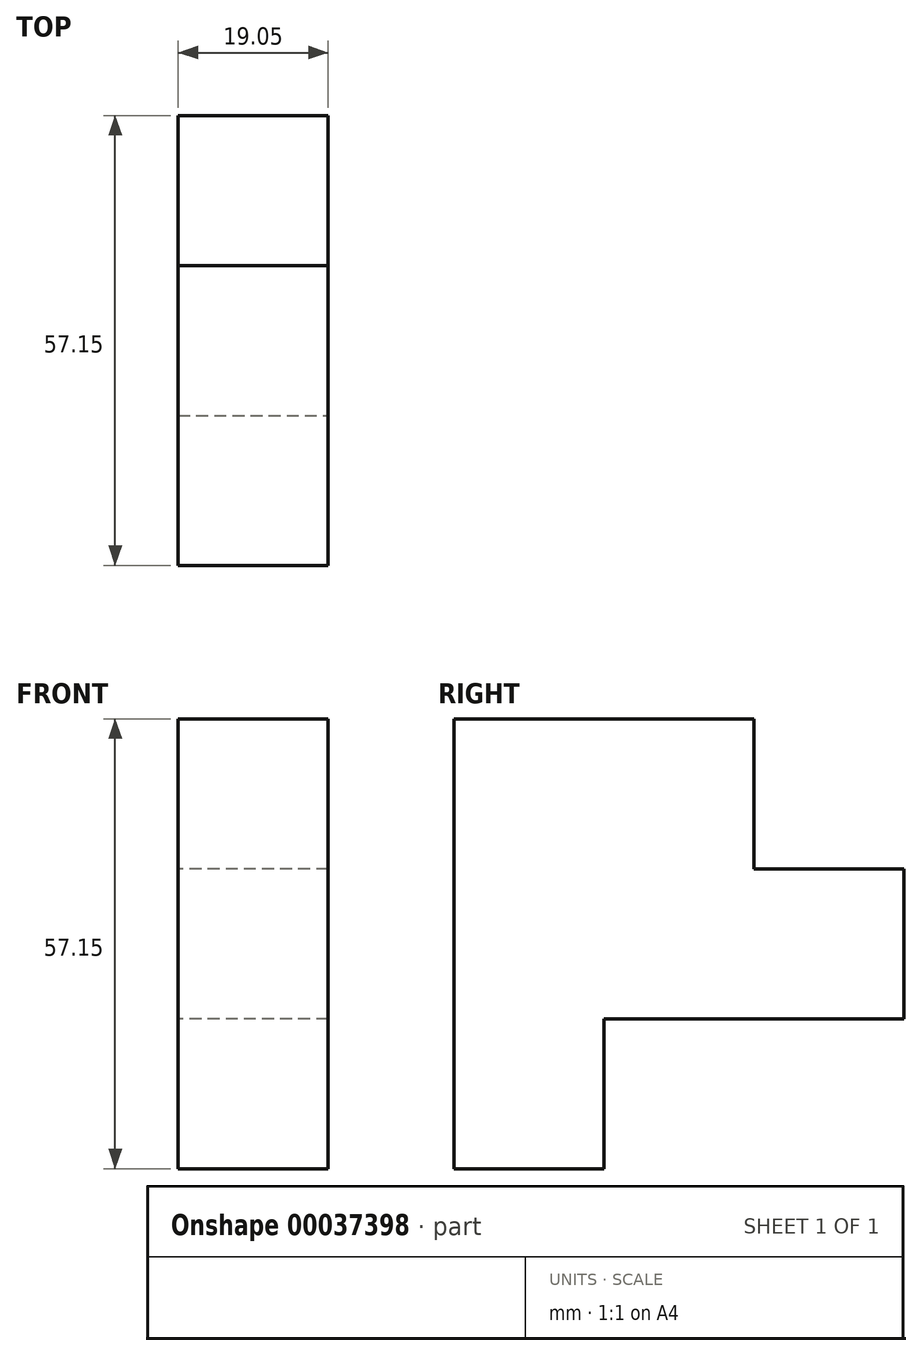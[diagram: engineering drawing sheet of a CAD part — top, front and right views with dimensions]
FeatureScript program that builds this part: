
annotation { "Feature Type Name" : "Feature", "Feature Type Description" : "" }
export const myFeature = defineFeature(function(context is Context, id is Id, definition is map)
    precondition{}
    {
        {
            var Q0;
            Q0=qCreatedBy(makeId("Top.planeOp"),FACE);
            var sketch = newSketch(context, id + "F0", { "sketchPlane" : qUnion([Q0])});
            skLineSegment(sketch, "E0.bottom", {"start": v(0, 0) * mm, "end": v(19.05, 0) * mm});
            skLineSegment(sketch, "E0.top", {"start": v(0, 57.15) * mm, "end": v(19.05, 57.15) * mm});
            skLineSegment(sketch, "E0.left", {"start": v(0, 0) * mm, "end": v(0, 57.15) * mm});
            skLineSegment(sketch, "E0.right", {"start": v(19.05, 0) * mm, "end": v(19.05, 57.15) * mm});
            skSolve(sketch);
        }
        {
            var Q0;
            Q0 = qSketchRegion(id + "F0", true);
            extrude(context, id + "F1", {"entities" : qUnion([Q0]), "depth" : 57.15 * mm});
        }
        {
            var Q0;
            Q0=makeQuery(id+"F1.opExtrude","SWEPT_FACE",FACE,{"disambiguationData":[OSD([sQuery(id+"F0.wireOp",EDGE,"E0.top")])]});
            var sketch = newSketch(context, id + "F2", { "sketchPlane" : qUnion([Q0])});
            skLineSegment(sketch, "E1.bottom", {"start": v(-19.05, 0) * mm, "end": v(0, 0) * mm});
            skLineSegment(sketch, "E1.top", {"start": v(-19.05, 19.05) * mm, "end": v(0, 19.05) * mm});
            skLineSegment(sketch, "E1.left", {"start": v(-19.05, 0) * mm, "end": v(-19.05, 19.05) * mm});
            skLineSegment(sketch, "E1.right", {"start": v(0, 0) * mm, "end": v(0, 19.05) * mm});
            skSolve(sketch);
        }
        {
            var Q0;
            Q0 = qSketchRegion(id + "F2", true);
            extrude(context, id + "F3", {"entities" : qUnion([Q0]), "operationType" : NewBodyOperationType.REMOVE, "oppositeDirection" : true, "depth" : 38.1 * mm});
        }
        {
            var Q0;
            Q0=makeQuery(id+"F1.opExtrude","SWEPT_FACE",FACE,{"disambiguationData":[OSD([sQuery(id+"F0.wireOp",EDGE,"E0.top")])]});
            var sketch = newSketch(context, id + "F4", { "sketchPlane" : qUnion([Q0])});
            skLineSegment(sketch, "E2.bottom", {"start": v(-19.05, 57.15) * mm, "end": v(0, 57.15) * mm});
            skLineSegment(sketch, "E2.top", {"start": v(-19.05, 38.1) * mm, "end": v(0, 38.1) * mm});
            skLineSegment(sketch, "E2.left", {"start": v(-19.05, 57.15) * mm, "end": v(-19.05, 38.1) * mm});
            skLineSegment(sketch, "E2.right", {"start": v(0, 57.15) * mm, "end": v(0, 38.1) * mm});
            skSolve(sketch);
        }
        {
            var Q0;
            Q0 = qSketchRegion(id + "F4", true);
            extrude(context, id + "F5", {"entities" : qUnion([Q0]), "operationType" : NewBodyOperationType.REMOVE, "oppositeDirection" : true, "depth" : 19.05 * mm});
        }
    });
